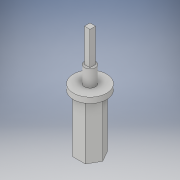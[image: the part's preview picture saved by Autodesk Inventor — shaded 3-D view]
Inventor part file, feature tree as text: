
AUTODESK INVENTOR PART (.ipt)
format: ipt  version: 2019 (Build 230136000, 136)  size: 132,608 bytes
history: native  units: in
note: dims shown in document units (in); Inventor stores cm internally (conversion verified against a paired STEP export)
features: extrude x4, sketch x4
ambient origin geometry x8: Origin, YZ Plane, XZ Plane, XY Plane, X Axis, Y Axis, Z Axis, Center Point
bodies: Solid1 (feature_tree)
feature tree (8):
  extrude  "Extrusion1"  TaperAngle=0.0deg  [1 undecoded]
  extrude  "Extrusion2"  Depth=0.75in
  extrude  "Extrusion3"  Depth=0.125in
  extrude  "Extrusion4"  Depth=0.125in
  sketch  "Sketch1"  dims[d0=0.5in d1=0.0in]
  sketch  "Sketch2"  dims[d2=1.25in d3=0.0in d4=0.75in]
  sketch  "Sketch3"  dims[d5=0.125in d6=0.0in d7=0.25in]
  sketch  "Sketch4"  dims[d8=0.375in d9=0.0in d10=0.125in d11=0.125in d12=0.75in d13=0.0in]
note: 1 required parameter value undecoded (feature->parameter linkage not recoverable at this tier; creation-order binding heuristic only, values carry confidence <= 0.55)
